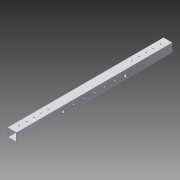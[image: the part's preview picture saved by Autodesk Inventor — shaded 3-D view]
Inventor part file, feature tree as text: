
AUTODESK INVENTOR PART (.ipt)
format: ipt  version: 2015 (Build 190159000, 159)  size: 194,048 bytes
history: native  units: in
note: dims shown in document units (in); Inventor stores cm internally (conversion verified against a paired STEP export)
features: other x4, hole x3, projected_geometry x2, extrude x1
ambient origin geometry x8: Origin, YZ Plane, XZ Plane, XY Plane, X Axis, Y Axis, Z Axis, Center Point
bodies: Solid1 (feature_tree)
feature tree (10):
  extrude  "profile_extrusion"  Depth=1.0in
  hole  "tb_rivet_holes"  [1 undecoded]
  hole  "bh_rivet_holes"  [1 undecoded]
  hole  "pdb_ziptie_holes"  [1 undecoded]
  other  "profile_sketch"
  other  "rivet_holes_sketch"
  other  "bh_rivet_holes_sketch"
  projected_geometry  "Projected Loop1"
  other  "pdb_ziptie_sketch"
  projected_geometry  "Projected Loop2"
note: 3 required parameter values undecoded (feature->parameter linkage not recoverable at this tier; creation-order binding heuristic only, values carry confidence <= 0.55)
